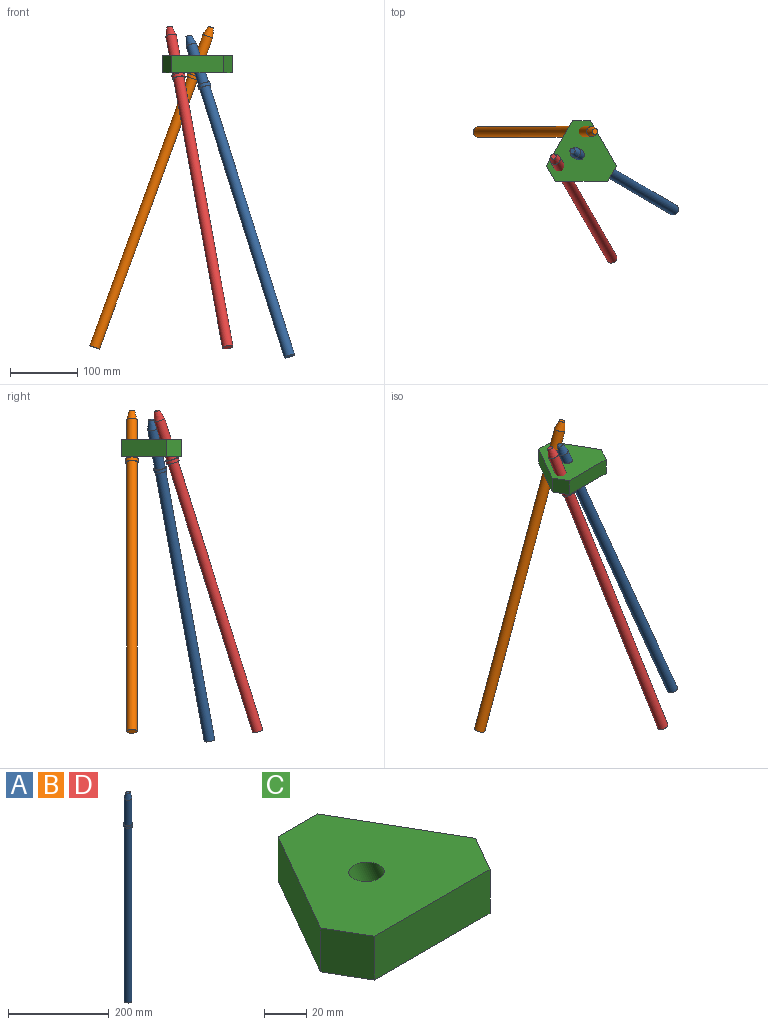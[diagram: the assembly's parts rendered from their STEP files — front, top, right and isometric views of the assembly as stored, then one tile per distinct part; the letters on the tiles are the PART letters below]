
ASSEMBLY  parts=4 mates=1
PART A: 8 faces, bbox 19.1x19.1x508 mm
  f0: cylinder r=7.87mm len=61.98mm, axis (0,0,-1), area 3066.4mm2, adj f2,f4
  f1: plane 8.13x8.13mm, normal (0,0,1), area 51.9mm2, adj f2
  f2: cone r=4.06mm half-angle=15deg, axis (0,0,-1), area 552.1mm2, adj f0,f1
  f3: cylinder r=9.53mm len=19.05mm, axis (0,0,-1), area 304mm2, adj f4,f5
  f4: plane 19.05x19.05mm, normal (0,0,1), area 90.2mm2, adj f0,f3
  f5: plane 19.05x19.05mm, normal (0,0,-1), area 90.2mm2, adj f3,f7
  f6: plane 15.75x15.75mm, normal (0,0,-1), area 194.8mm2, adj f7
  f7: cylinder r=7.87mm len=426.72mm, axis (0,0,-1), area 21111.5mm2, adj f5,f6
PART B: same geometry as A
PART C: 9 faces, bbox 103.9x90x36.3 mm
  f0: plane 67.1x38.74mm, normal (-0.87,0.5,0), area 1968mm2, adj f1,f5,f6,f7
  f1: plane 25.4x22.86mm, normal (-0.87,-0.5,0), area 670.3mm2, adj f0,f2,f6,f7
  f2: plane 77.48x25.4mm, normal (0,-1,0), area 1968mm2, adj f1,f3,f6,f7
  f3: plane 25.4x22.86mm, normal (0.87,-0.5,0), area 670.3mm2, adj f2,f4,f6,f7
  f4: plane 67.1x38.74mm, normal (0.87,0.5,0), area 1968mm2, adj f3,f5,f6,f7
  f5: plane 26.39x25.4mm, normal (0,1,0), area 670.3mm2, adj f0,f4,f6,f7
  f6: plane 103.87x89.96mm, normal (0,0,1), area 6232.2mm2, adj f0,f1,f2,f3,f4,f5,f8
  f7: plane 103.87x89.96mm, normal (0,0,-1), area 6232.2mm2, adj f0,f1,f2,f3,f4,f5,f8
  f8: cylinder r=7.94mm len=36.3mm, axis (-0.3,0.17,0.94), area 1348.1mm2, adj f6,f7
PART D: same geometry as A
PLACE A rot(axis=(-0.45,-0.86,-0.24),20.6deg) t=(136.66,-86.62,-434.8)mm
PLACE B rot(axis=(0,1,0),20deg) t=(-154.1,29.04,-421.64)mm
PLACE C t=(-0.5,-7.43,-12.35)mm fixed
PLACE D rot(axis=(-0.87,-0.49,0.07),20.1deg) t=(44.64,-158.59,-421.32)mm
MATE cylindrical A.f0 <-> C.f8  axis (0.3,-0.17,-0.94) through (-0.42,-7.48,0.08)mm
